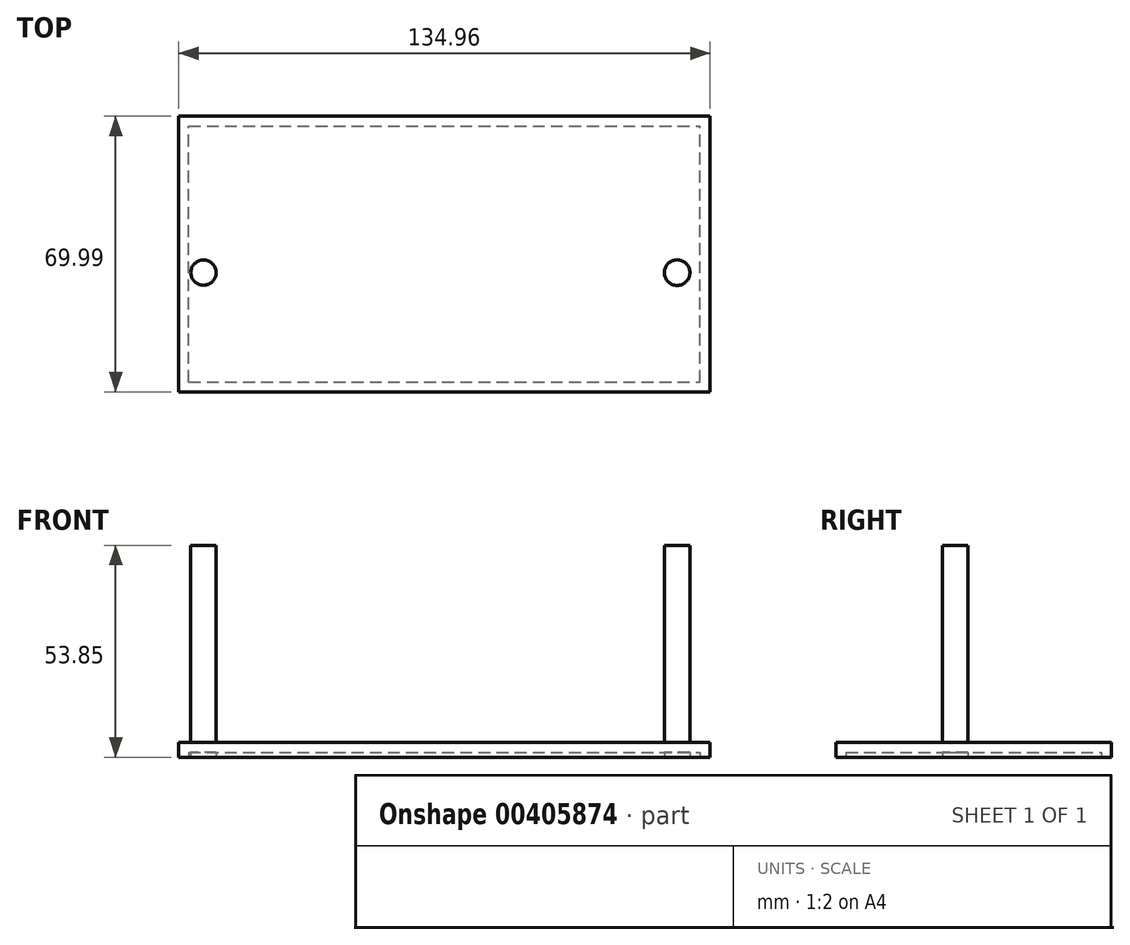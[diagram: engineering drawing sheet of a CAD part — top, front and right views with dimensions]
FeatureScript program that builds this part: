
annotation { "Feature Type Name" : "Feature", "Feature Type Description" : "" }
export const myFeature = defineFeature(function(context is Context, id is Id, definition is map)
    precondition{}
    {
        {
            var Q0;
            Q0=qCreatedBy(makeId("Top.planeOp"),FACE);
            var sketch = newSketch(context, id + "F0", { "sketchPlane" : qUnion([Q0])});
            skLineSegment(sketch, "E0.bottom", {"start": v(-66.13, -30.27) * mm, "end": v(68.83, -30.27) * mm});
            skLineSegment(sketch, "E0.top", {"start": v(-66.13, 39.72) * mm, "end": v(68.83, 39.72) * mm});
            skLineSegment(sketch, "E0.left", {"start": v(-66.13, -30.27) * mm, "end": v(-66.13, 39.72) * mm});
            skLineSegment(sketch, "E0.right", {"start": v(68.83, -30.27) * mm, "end": v(68.83, 39.72) * mm});
            skSolve(sketch);
        }
        {
            var Q0;
            Q0=makeQuery(id+"F0.imprint","IMPRINT",FACE,{"disambiguationData":[TD([[makeQuery(id+"F0.imprint","IMPRINT",EDGE,{"derivedFrom":sQuery(id+"F0.wireOp",EDGE,"E0.bottom")}),1.0]])]});
            extrude(context, id + "F1", {"entities" : qUnion([Q0]), "depth" : 3.8 * mm});
        }
        {
            var Q0;
            Q0=makeQuery(id+"F1.opExtrude","CAP_FACE",FACE,{"disambiguationData":[OSD([sQuery(id+"F0.wireOp",EDGE,"E0.bottom"),sQuery(id+"F0.wireOp",EDGE,"E0.top"),sQuery(id+"F0.wireOp",EDGE,"E0.left"),sQuery(id+"F0.wireOp",EDGE,"E0.right")])],"isStart":true});
            shell(context, id + "F2", {"entities" : qUnion([Q0]), "thickness" : 2.54 * mm});
        }
        {
            var Q0;
            Q0=qCreatedBy(makeId("Top.planeOp"),FACE);
            var sketch = newSketch(context, id + "F3", { "sketchPlane" : qUnion([Q0])});
            skCircle(sketch, "E1", {"center": v(-59.86, 0) * mm, "radius": 3.22 * mm});
            skCircle(sketch, "E2", {"center": v(60.47, 0) * mm, "radius": 3.26 * mm});
            skSolve(sketch);
        }
        {
            var Q0;
            Q0=makeQuery(id+"F3.imprint","IMPRINT",FACE,{"disambiguationData":[TD([[makeQuery(id+"F3.imprint","IMPRINT",EDGE,{"derivedFrom":sQuery(id+"F3.wireOp",EDGE,"E1")}),1.0]])]});
            var Q1;
            Q1=makeQuery(id+"F3.imprint","IMPRINT",FACE,{"disambiguationData":[TD([[makeQuery(id+"F3.imprint","IMPRINT",EDGE,{"derivedFrom":sQuery(id+"F3.wireOp",EDGE,"E2")}),1.0]])]});
            extrude(context, id + "F4", {"entities" : qUnion([Q0, Q1]), "operationType" : NewBodyOperationType.ADD, "depth" : 53.85 * mm});
        }
    });
